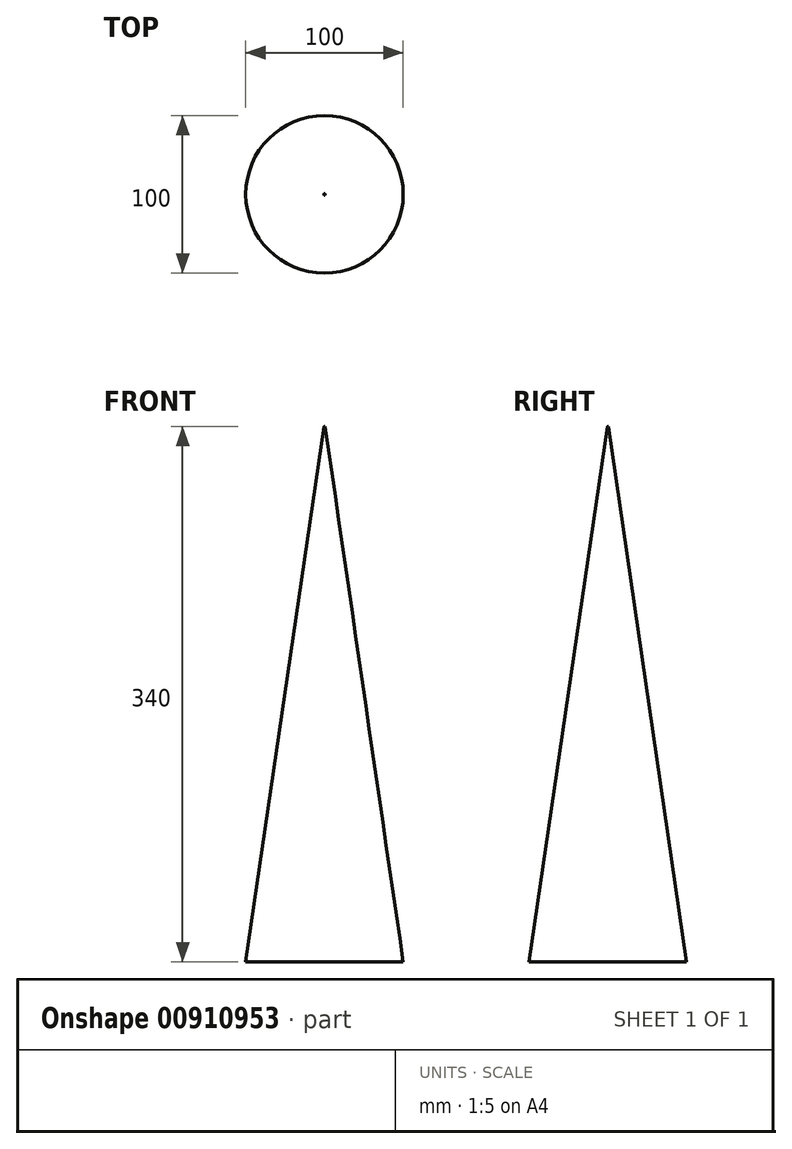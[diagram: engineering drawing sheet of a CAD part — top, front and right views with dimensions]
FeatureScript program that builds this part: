
annotation { "Feature Type Name" : "Feature", "Feature Type Description" : "" }
export const myFeature = defineFeature(function(context is Context, id is Id, definition is map)
    precondition{}
    {
        {
            var Q0;
            Q0=qCreatedBy(makeId("Top.planeOp"),FACE);
            var sketch = newSketch(context, id + "F0", { "sketchPlane" : qUnion([Q0])});
            skCircle(sketch, "E0", {"center": v(0, 0) * mm, "radius": 50 * mm});
            skSolve(sketch);
        }
        {
            var Q0;
            Q0=makeQuery(id+"F0.imprint","IMPRINT",FACE,{"disambiguationData":[TD([[makeQuery(id+"F0.imprint","IMPRINT",EDGE,{"derivedFrom":sQuery(id+"F0.wireOp",EDGE,"E0")}),1.0]])]});
            extrude(context, id + "F1", {"entities" : qUnion([Q0]), "depth" : 340 * mm, "offsetDistance" : 25 * mm, "hasDraft" : true, "draftAngle" : 8.3 * degree, "draftPullDirection" : true});
        }
    });
